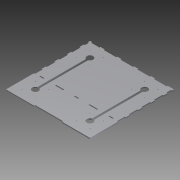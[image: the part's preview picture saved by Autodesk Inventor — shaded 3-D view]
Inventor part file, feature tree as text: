
AUTODESK INVENTOR PART (.ipt)
format: ipt  version: 2011 (Build 150239000, 239)  size: 1,099,776 bytes
history: native  units: in
note: dims shown in document units (in); Inventor stores cm internally (conversion verified against a paired STEP export)
features: sketch x33, extrude x32, fillet x2
ambient origin geometry x8: Origin, YZ Plane, XZ Plane, XY Plane, X Axis, Y Axis, Z Axis, Center Point
bodies: Solid1 (feature_tree)
feature tree (67):
  sketch  "Sketch1"  dims[d0=20.0in d1=20.0in]
  extrude  "Extrusion1"  Depth=20.0in
  extrude  "Extrusion2"  Depth=3.5in
  extrude  "Extrusion3"  Depth=3.5in
  extrude  "Extrusion4"  Depth=3.5in
  extrude  "Extrusion5"  Depth=3.5in
  extrude  "Extrusion6"  Depth=1.911in
  extrude  "Extrusion7"  Depth=5.089in
  extrude  "Extrusion8"  Depth=5.089in
  extrude  "Extrusion9"  Depth=1.911in
  extrude  "Extrusion10"  Depth=0.156in
  extrude  "Extrusion11"  Depth=0.156in
  extrude  "Extrusion12"  Depth=0.156in
  extrude  "Extrusion13"  Depth=0.156in
  extrude  "Extrusion14"  Depth=0.156in
  extrude  "Extrusion15"  Depth=0.156in
  fillet  "Fillet1"  Radius=0.156in
  fillet  "Fillet2"  Radius=0.156in
  extrude  "Extrusion16"  Depth=0.156in
  extrude  "Extrusion17"  Depth=1.0in
  extrude  "Extrusion18"  Depth=1.0in
  extrude  "Extrusion19"  Depth=0.5in TaperAngle=0.0deg
  extrude  "Extrusion20"  Depth=0.5in
  extrude  "Extrusion21"  Depth=1.5in
  extrude  "Extrusion22"  Depth=1.5in
  extrude  "Extrusion23"  Depth=1.5in
  extrude  "Extrusion24"  Depth=1.5in
  extrude  "Extrusion25"  Depth=1.5in
  extrude  "Extrusion26"  Depth=1.5in
  extrude  "Extrusion27"  Depth=1.5in
  extrude  "Extrusion28"  Depth=1.0in TaperAngle=0.0deg
  extrude  "Extrusion29"  Depth=0.5in TaperAngle=0.0deg
  extrude  "Extrusion30"  Depth=0.25in TaperAngle=0.0deg
  extrude  "Extrusion31"  Depth=2.6in
  extrude  "Extrusion32"  Depth=7.4in
  sketch  "Sketch2"  dims[d2=3.5in d3=3.5in]
  sketch  "Sketch3"  dims[d4=3.5in d5=3.5in]
  sketch  "Sketch4"  dims[d6=3.5in d7=3.5in]
  sketch  "Sketch5"  dims[d8=3.5in d9=3.5in]
  sketch  "Sketch6"  dims[d10=1.911in d11=1.911in]
  sketch  "Sketch7"  dims[d12=1.911in d13=5.089in]
  sketch  "Sketch8"  dims[d14=5.089in d15=5.089in]
  sketch  "Sketch9"  dims[d16=5.089in d17=1.911in]
  sketch  "Sketch10"  dims[d18=1.911in d19=0.156in]
  sketch  "Sketch11"  dims[d20=0.156in d21=0.156in]
  sketch  "Sketch12"  dims[d22=0.156in d23=0.156in]
  sketch  "Sketch13"  dims[d24=0.156in d25=0.156in]
  sketch  "Sketch14"  dims[d26=0.156in d27=0.156in]
  sketch  "Sketch15"  dims[d28=0.156in d29=0.156in d30=0.156in d31=0.156in]
  sketch  "Sketch16"  dims[d32=0.156in d33=0.156in]
  sketch  "Sketch17"  dims[d34=0.156in d35=1.0in]
  sketch  "Sketch18"  dims[d36=1.0in d37=1.0in]
  sketch  "Sketch19"  dims[d38=1.0in d39=0.5in d40=0.0in]
  sketch  "Sketch20"  dims[d41=0.5in d42=0.5in]
  sketch  "Sketch21"  dims[d43=1.0in d44=1.5in]
  sketch  "Sketch22"  dims[d45=1.0in d46=1.5in]
  sketch  "Sketch23"  dims[d47=1.0in d48=1.5in]
  sketch  "Sketch24"  dims[d49=1.0in d50=1.5in]
  sketch  "Sketch25"  dims[d51=1.0in d52=1.5in]
  sketch  "Sketch26"  dims[d53=1.0in d54=1.5in]
  sketch  "Sketch27"  dims[d55=1.0in d56=1.5in]
  sketch  "Sketch28"  dims[d57=1.0in d58=1.0in d59=0.0in]
  sketch  "Sketch29"  dims[d60=1.0in d61=0.0in d62=0.5in d63=0.0in]
  sketch  "Sketch30"  dims[d64=0.5in d65=0.0in d66=0.25in d67=0.0in]
  sketch  "Sketch31"  dims[d68=10.0in d69=2.6in]
  sketch  "Sketch32"  dims[d70=5.2in d71=7.4in]
  sketch  "Sketch33"  dims[d72=5.2in d73=0.25in d74=0.25in d75=0.25in d76=0.25in d77=0.25in d78=0.25in d79=0.25in d80=0.25in d81=0.25in d82=0.25in d83=0.25in d84=0.25in d85=0.25in d86=0.0in d87=1.5in d88=1.5in d89=1.5in d90=1.5in d91=0.25in d92=0.25in d93=0.25in d94=0.25in d95=0.25in d96=0.25in d97=0.25in d98=0.25in d99=0.25in d100=0.25in d101=0.25in d102=0.25in d103=0.0in d104=0.25in d105=0.0in d106=1.0in d107=1.0in d108=1.0in d109=1.0in d110=1.0in d111=1.0in d112=1.0in d113=1.0in d114=1.0in d115=1.0in d116=1.0in d117=1.0in d118=1.0in d119=1.0in d120=1.0in d121=1.0in d122=1.0in d123=1.0in d124=1.0in d125=1.0in d126=0.25in d127=1.0in d128=0.0in d129=1.0in d130=0.0in d131=1.0in d132=0.0in d133=0.5in d134=0.5in d135=0.5in d136=0.5in d137=1.0in d138=0.0in d139=1.5in d140=0.25in d141=0.0in d142=0.125in d143=0.25in d144=0.125in d145=0.25in d146=0.25in d147=0.0in d148=0.5in d149=0.5in d150=0.25in d151=0.5in d152=1.0in d153=0.0in d154=0.25in d155=0.5in d156=1.0in d157=0.0in d158=6.45in d159=0.25in d160=0.0in d161=1.25in d162=1.0in d163=2.0in d164=1.0in d165=2.0in d166=1.0in d167=2.0in d168=1.0in d169=0.25in d170=0.0in d171=0.5in d172=0.25in d173=0.0in d174=0.25in d175=0.25in d176=1.0in d177=3.0in d178=1.0in d179=3.0in d180=1.0in d181=3.0in d182=1.0in d183=3.0in d184=1.0in d185=0.25in d186=0.0in d187=0.5in d188=0.5in d189=0.25in d190=0.0in d191=0.25in d192=0.0in d193=0.25in d194=0.0in d195=1.0in d196=0.25in d197=1.0in d198=1.0in d199=1.0in d200=1.75in d201=1.0in d202=1.75in d203=1.0in d204=3.0in d205=1.0in d206=0.25in d207=0.0in d208=0.5in d209=2.0in d210=0.5in d211=2.0in d212=0.25in d213=0.0in d214=0.25in d215=0.0in d216=0.25in d217=0.0in d218=0.25in d219=0.0in d220=1.594in d221=1.594in d222=3.188in d223=3.188in d224=1.594in d225=1.594in d226=3.188in d227=3.188in d228=0.156in d229=0.156in d230=0.156in d231=0.156in d232=0.156in d233=0.156in d234=0.156in d235=0.156in d236=0.25in d237=0.0in d238=0.25in d239=0.0in d240=3.188in d241=0.25in d242=0.0in]
